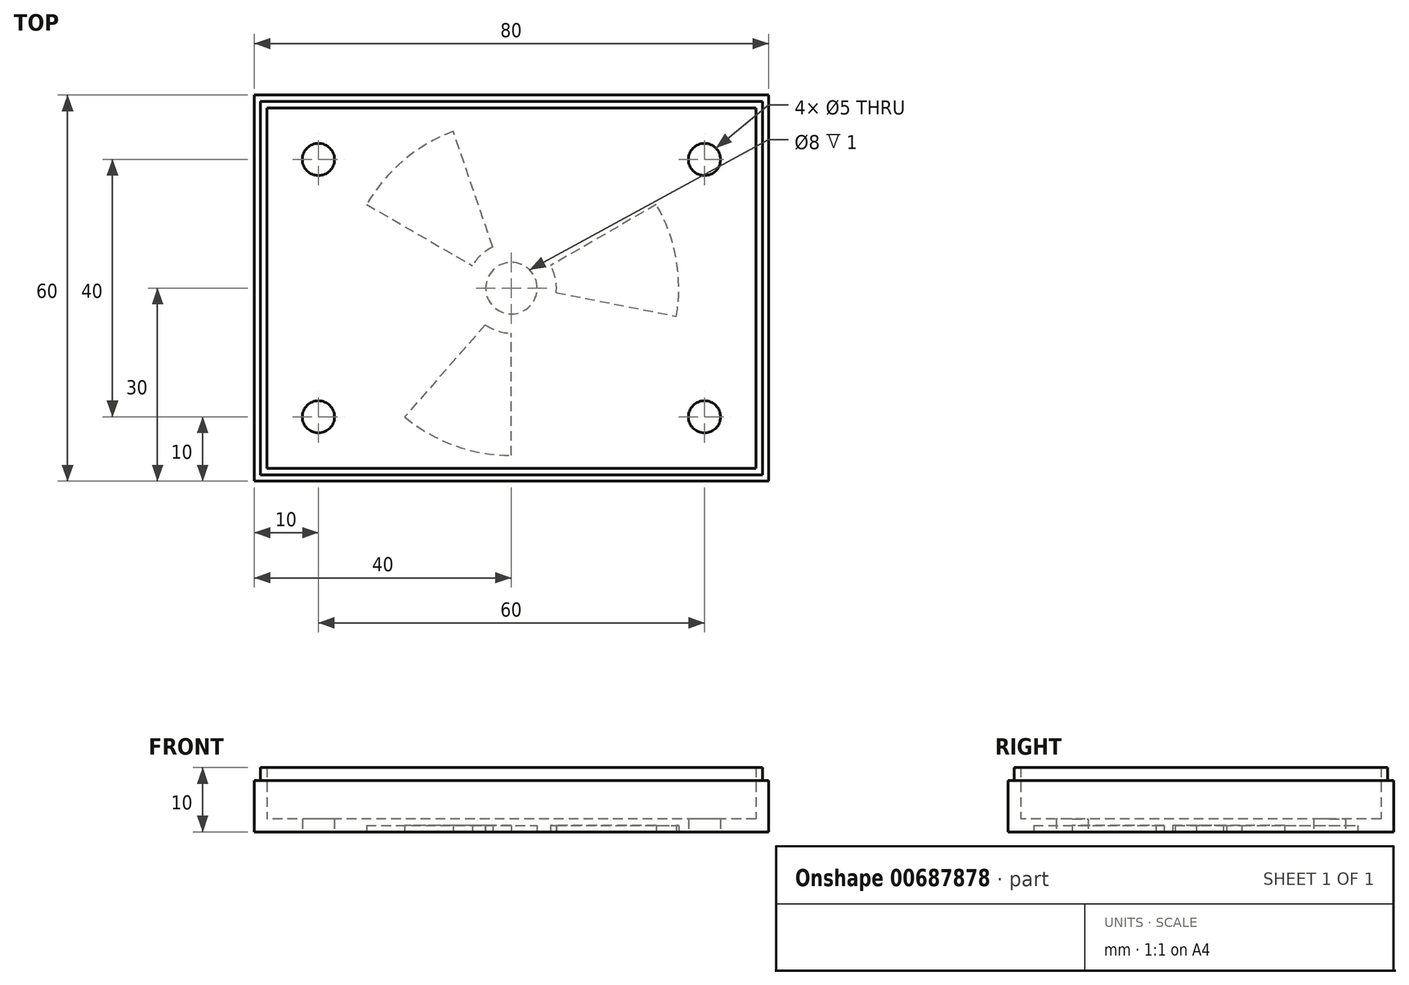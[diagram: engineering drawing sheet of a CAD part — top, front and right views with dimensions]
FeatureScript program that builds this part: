
annotation { "Feature Type Name" : "Feature", "Feature Type Description" : "" }
export const myFeature = defineFeature(function(context is Context, id is Id, definition is map)
    precondition{}
    {
        {
            var Q0;
            Q0=qCreatedBy(makeId("Top.planeOp"),FACE);
            var sketch = newSketch(context, id + "F0", { "sketchPlane" : qUnion([Q0])});
            skLineSegment(sketch, "E0.bottom", {"start": v(40, 30) * mm, "end": v(-40, 30) * mm});
            skLineSegment(sketch, "E0.top", {"start": v(40, -30) * mm, "end": v(-40, -30) * mm});
            skLineSegment(sketch, "E0.left", {"start": v(40, 30) * mm, "end": v(40, -30) * mm});
            skLineSegment(sketch, "E0.right", {"start": v(-40, 30) * mm, "end": v(-40, -30) * mm});
            skPoint(sketch, "E0.middle", {"position": v(0, 0) * mm});
            skSolve(sketch);
        }
        {
            var Q0;
            Q0 = qSketchRegion(id + "F0", true);
            extrude(context, id + "F1", {"entities" : qUnion([Q0]), "depth" : 10 * mm, "offsetDistance" : 25 * mm});
        }
        {
            var Q0;
            Q0=makeQuery(id+"F1.opExtrude","CAP_FACE",FACE,{"disambiguationData":[OSD([sQuery(id+"F0.wireOp",EDGE,"E0.bottom"),sQuery(id+"F0.wireOp",EDGE,"E0.top"),sQuery(id+"F0.wireOp",EDGE,"E0.left"),sQuery(id+"F0.wireOp",EDGE,"E0.right")])],"isStart":false});
            shell(context, id + "F2", {"entities" : qUnion([Q0]), "thickness" : 2 * mm});
        }
        {
            var Q0;
            Q0=makeQuery(id+"F1.opExtrude","CAP_FACE",FACE,{"disambiguationData":[OSD([sQuery(id+"F0.wireOp",EDGE,"E0.bottom"),sQuery(id+"F0.wireOp",EDGE,"E0.top"),sQuery(id+"F0.wireOp",EDGE,"E0.left"),sQuery(id+"F0.wireOp",EDGE,"E0.right")])],"isStart":false});
            var sketch = newSketch(context, id + "F3", { "sketchPlane" : qUnion([Q0])});
            skLineSegment(sketch, "E1.0", {"start": v(39, 29) * mm, "end": v(-39, 29) * mm});
            skLineSegment(sketch, "E1.1", {"start": v(39, 29) * mm, "end": v(39, -29) * mm});
            skLineSegment(sketch, "E1.2", {"start": v(39, -29) * mm, "end": v(-39, -29) * mm});
            skLineSegment(sketch, "E1.3", {"start": v(-39, 29) * mm, "end": v(-39, -29) * mm});
            skLineSegment(sketch, "E2.0", {"start": v(40, 30) * mm, "end": v(-40, 30) * mm});
            skLineSegment(sketch, "E2.1", {"start": v(40, 30) * mm, "end": v(40, -30) * mm});
            skLineSegment(sketch, "E2.2", {"start": v(40, -30) * mm, "end": v(-40, -30) * mm});
            skLineSegment(sketch, "E2.3", {"start": v(-40, 30) * mm, "end": v(-40, -30) * mm});
            skSolve(sketch);
        }
        {
            var Q0;
            Q0 = qSketchRegion(id + "F3", true);
            extrude(context, id + "F4", {"entities" : qUnion([Q0]), "operationType" : NewBodyOperationType.REMOVE, "oppositeDirection" : true, "depth" : 2 * mm, "offsetDistance" : 25 * mm});
        }
        {
            var Q0;
            Q0=makeQuery(id+"F1.opExtrude","CAP_FACE",FACE,{"disambiguationData":[OSD([sQuery(id+"F0.wireOp",EDGE,"E0.bottom"),sQuery(id+"F0.wireOp",EDGE,"E0.top"),sQuery(id+"F0.wireOp",EDGE,"E0.left"),sQuery(id+"F0.wireOp",EDGE,"E0.right")])],"isStart":true});
            var sketch = newSketch(context, id + "F5", { "sketchPlane" : qUnion([Q0])});
            skCircle(sketch, "E3", {"center": v(-30, 20) * mm, "radius": 2.5 * mm});
            skCircle(sketch, "E4", {"center": v(30, -20) * mm, "radius": 2.5 * mm});
            skCircle(sketch, "E5", {"center": v(30, 20) * mm, "radius": 2.5 * mm});
            skCircle(sketch, "E6", {"center": v(-30, -20) * mm, "radius": 2.5 * mm});
            skSolve(sketch);
        }
        {
            var Q0;
            Q0 = qSketchRegion(id + "F5", true);
            extrude(context, id + "F6", {"entities" : qUnion([Q0]), "operationType" : NewBodyOperationType.REMOVE, "oppositeDirection" : true, "depth" : 25 * mm, "offsetDistance" : 25 * mm});
        }
        {
            var Q0;
            Q0=makeQuery(id+"F1.opExtrude","CAP_FACE",FACE,{"disambiguationData":[OSD([sQuery(id+"F0.wireOp",EDGE,"E0.bottom"),sQuery(id+"F0.wireOp",EDGE,"E0.top"),sQuery(id+"F0.wireOp",EDGE,"E0.left"),sQuery(id+"F0.wireOp",EDGE,"E0.right")])],"isStart":true});
            var sketch = newSketch(context, id + "F7", { "sketchPlane" : qUnion([Q0])});
            skCircle(sketch, "E7", {"center": v(0, 0) * mm, "radius": 4 * mm});
            skArc(sketch, "E8", {"start": v(-4.07, 5.7) * mm, "mid": v(-2.14, 6.67) * mm, "end": v(0, 7) * mm});
            skArc(sketch, "E9", {"start": v(-16.6, 20.01) * mm, "mid": v(-8.82, 24.46) * mm, "end": v(0, 26) * mm});
            skLineSegment(sketch, "E10", {"start": v(0, 26) * mm, "end": v(0, 7) * mm});
            skLineSegment(sketch, "E11", {"start": v(-4.07, 5.7) * mm, "end": v(-16.6, 20.01) * mm});
            skSolve(sketch);
        }
        {
            var Q0;
            Q0 = qSketchRegion(id + "F7", true);
            extrude(context, id + "F8", {"entities" : qUnion([Q0]), "oppositeDirection" : true, "depth" : 1 * mm, "offsetDistance" : 25 * mm});
        }
        {
            var Q0;
            Q0=qCreatedBy(makeId("Front.planeOp"),FACE);
            var sketch = newSketch(context, id + "F9", { "sketchPlane" : qUnion([Q0])});
            skLineSegment(sketch, "E12", {"start": v(0, 36.07) * mm, "end": v(0, -35.21) * mm});
            skSolve(sketch);
        }
        {
            var Q0;
            Q0=makeQuery(id+"F8.opExtrude","SWEPT_BODY",BODY,{"disambiguationData":[OSD([sQuery(id+"F7.wireOp",EDGE,"E8"),sQuery(id+"F7.wireOp",EDGE,"E9"),sQuery(id+"F7.wireOp",EDGE,"E10"),sQuery(id+"F7.wireOp",EDGE,"E11")])]});
            var Q1;
            Q1=sQuery(id+"F9.wireOp",EDGE,"E12");
            circularPattern(context, id + "F10", {"entities" : qUnion([Q0]), "axis" : qUnion([Q1]), "angle" : 360 * degree, "instanceCount" : 3, "equalSpace" : true});
        }
        {
            var Q0;
            Q0=makeQuery(id+"F8.opExtrude","SWEPT_BODY",BODY,{"disambiguationData":[OSD([sQuery(id+"F7.wireOp",EDGE,"E7")])]});
            var Q1;
            Q1=makeQuery(id+"F10.opPattern","COPY",BODY,{"derivedFrom":makeQuery(id+"F8.opExtrude","SWEPT_BODY",BODY,{"disambiguationData":[OSD([sQuery(id+"F7.wireOp",EDGE,"E8"),sQuery(id+"F7.wireOp",EDGE,"E9"),sQuery(id+"F7.wireOp",EDGE,"E10"),sQuery(id+"F7.wireOp",EDGE,"E11")])]}),"instanceName":"1"});
            var Q2;
            Q2=makeQuery(id+"F8.opExtrude","SWEPT_BODY",BODY,{"disambiguationData":[OSD([sQuery(id+"F7.wireOp",EDGE,"E8"),sQuery(id+"F7.wireOp",EDGE,"E9"),sQuery(id+"F7.wireOp",EDGE,"E10"),sQuery(id+"F7.wireOp",EDGE,"E11")])]});
            var Q3;
            Q3=makeQuery(id+"F10.opPattern","COPY",BODY,{"derivedFrom":makeQuery(id+"F8.opExtrude","SWEPT_BODY",BODY,{"disambiguationData":[OSD([sQuery(id+"F7.wireOp",EDGE,"E8"),sQuery(id+"F7.wireOp",EDGE,"E9"),sQuery(id+"F7.wireOp",EDGE,"E10"),sQuery(id+"F7.wireOp",EDGE,"E11")])]}),"instanceName":"2"});
            var Q4;
            Q4=makeQuery(id+"F1.opExtrude","SWEPT_BODY",BODY,{"disambiguationData":[OSD([sQuery(id+"F0.wireOp",EDGE,"E0.bottom"),sQuery(id+"F0.wireOp",EDGE,"E0.top"),sQuery(id+"F0.wireOp",EDGE,"E0.left"),sQuery(id+"F0.wireOp",EDGE,"E0.right")])]});
            booleanBodies(context, id + "F11", {"operationType" : BooleanOperationType.SUBTRACTION, "tools" : qUnion([Q0, Q1, Q2, Q3]), "targets" : qUnion([Q4])});
        }
    });
